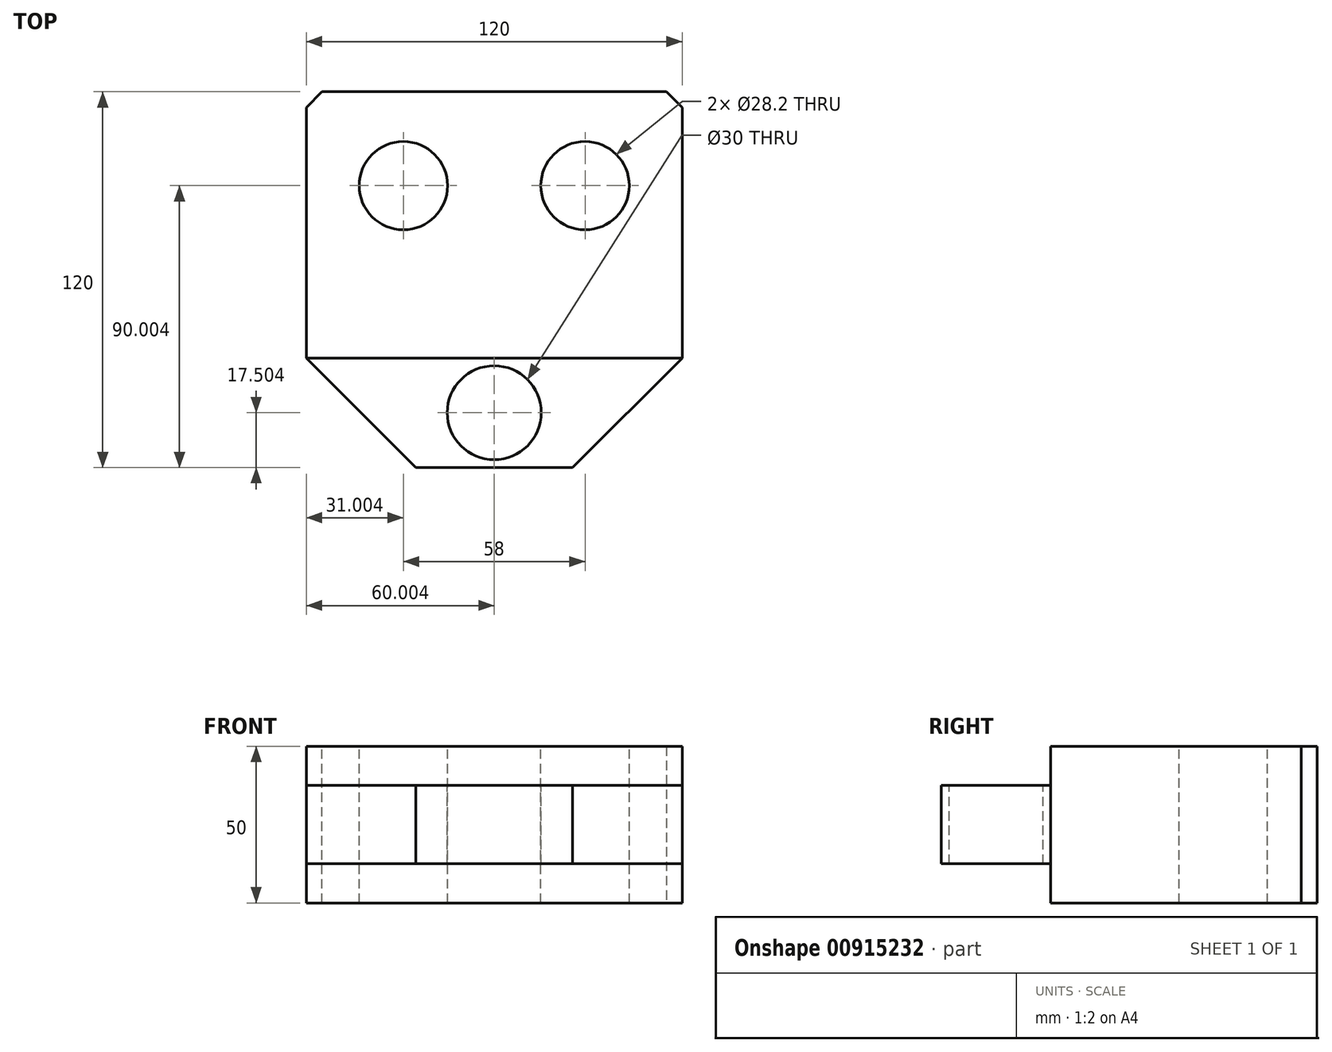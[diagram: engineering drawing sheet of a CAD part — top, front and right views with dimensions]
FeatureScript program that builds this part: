
annotation { "Feature Type Name" : "Feature", "Feature Type Description" : "" }
export const myFeature = defineFeature(function(context is Context, id is Id, definition is map)
    precondition{}
    {
        {
            var Q0;
            Q0=qCreatedBy(makeId("Top.planeOp"),FACE);
            var sketch = newSketch(context, id + "F0", { "sketchPlane" : qUnion([Q0])});
            skLineSegment(sketch, "E0.bottom", {"start": v(-56.18, 53.34) * mm, "end": v(63.82, 53.34) * mm});
            skLineSegment(sketch, "E0.top", {"start": v(-56.18, -66.66) * mm, "end": v(63.82, -66.66) * mm});
            skLineSegment(sketch, "E0.left", {"start": v(-56.18, 53.34) * mm, "end": v(-56.18, -66.66) * mm});
            skLineSegment(sketch, "E0.right", {"start": v(63.82, 53.34) * mm, "end": v(63.82, -66.66) * mm});
            skSolve(sketch);
        }
        {
            var Q0;
            Q0=makeQuery(id+"F0.imprint","IMPRINT",FACE,{"disambiguationData":[TD([[makeQuery(id+"F0.imprint","IMPRINT",EDGE,{"derivedFrom":sQuery(id+"F0.wireOp",EDGE,"E0.bottom")}),-1.0]])]});
            extrude(context, id + "F1", {"entities" : qUnion([Q0]), "depth" : 50 * mm, "offsetDistance" : 25 * mm});
        }
        {
            var Q0;
            Q0=makeQuery(id+"F1.opExtrude","SWEPT_EDGE",EDGE,{"disambiguationData":[OSD([sQuery(id+"F0.wireOp",EDGE,"E0.top"),sQuery(id+"F0.wireOp",EDGE,"E0.left")])]});
            var Q1;
            Q1=makeQuery(id+"F1.opExtrude","SWEPT_EDGE",EDGE,{"disambiguationData":[OSD([sQuery(id+"F0.wireOp",EDGE,"E0.top"),sQuery(id+"F0.wireOp",EDGE,"E0.right")])]});
            chamfer(context, id + "F2", {"entities" : qUnion([Q0, Q1]), "width" : 35 * mm, "tangentPropagation" : true});
        }
        {
            var Q0;
            Q0=makeQuery(id+"F1.opExtrude","CAP_FACE",FACE,{"disambiguationData":[OSD([sQuery(id+"F0.wireOp",EDGE,"E0.bottom"),sQuery(id+"F0.wireOp",EDGE,"E0.top"),sQuery(id+"F0.wireOp",EDGE,"E0.left"),sQuery(id+"F0.wireOp",EDGE,"E0.right")])],"isStart":false});
            var sketch = newSketch(context, id + "F3", { "sketchPlane" : qUnion([Q0])});
            skLineSegment(sketch, "E1", {"start": v(-56.18, -31.66) * mm, "end": v(63.82, -31.66) * mm});
            skLineSegment(sketch, "E2", {"start": v(63.82, -31.66) * mm, "end": v(28.82, -66.66) * mm});
            skLineSegment(sketch, "E3", {"start": v(28.82, -66.66) * mm, "end": v(-21.18, -66.66) * mm});
            skLineSegment(sketch, "E4", {"start": v(-21.18, -66.66) * mm, "end": v(-56.18, -31.66) * mm});
            skSolve(sketch);
        }
        {
            var Q0;
            Q0=makeQuery(id+"F3.imprint","IMPRINT",FACE,{"disambiguationData":[TD([[makeQuery(id+"F3.imprint","IMPRINT",EDGE,{"derivedFrom":sQuery(id+"F3.wireOp",EDGE,"E1")}),-1.0]])]});
            extrude(context, id + "F4", {"entities" : qUnion([Q0]), "operationType" : NewBodyOperationType.REMOVE, "oppositeDirection" : true, "depth" : 12.5 * mm, "offsetDistance" : 25 * mm});
        }
        {
            var Q0;
            Q0=makeQuery(id+"F1.opExtrude","CAP_FACE",FACE,{"disambiguationData":[OSD([sQuery(id+"F0.wireOp",EDGE,"E0.bottom"),sQuery(id+"F0.wireOp",EDGE,"E0.top"),sQuery(id+"F0.wireOp",EDGE,"E0.left"),sQuery(id+"F0.wireOp",EDGE,"E0.right")])],"isStart":true});
            var sketch = newSketch(context, id + "F5", { "sketchPlane" : qUnion([Q0])});
            skLineSegment(sketch, "E5", {"start": v(63.82, 31.66) * mm, "end": v(-56.18, 31.66) * mm});
            skLineSegment(sketch, "E6", {"start": v(-56.18, 31.66) * mm, "end": v(-21.18, 66.66) * mm});
            skLineSegment(sketch, "E7", {"start": v(-21.18, 66.66) * mm, "end": v(28.82, 66.66) * mm});
            skLineSegment(sketch, "E8", {"start": v(28.82, 66.66) * mm, "end": v(63.82, 31.66) * mm});
            skSolve(sketch);
        }
        {
            var Q0;
            Q0=makeQuery(id+"F5.imprint","IMPRINT",FACE,{"disambiguationData":[TD([[makeQuery(id+"F5.imprint","IMPRINT",EDGE,{"derivedFrom":sQuery(id+"F5.wireOp",EDGE,"E5")}),-1.0]])]});
            extrude(context, id + "F6", {"entities" : qUnion([Q0]), "operationType" : NewBodyOperationType.REMOVE, "oppositeDirection" : true, "depth" : 12.5 * mm, "offsetDistance" : 25 * mm});
        }
        {
            var Q0;
            Q0=makeQuery(id+"F4.boolean.opBoolean","COPY",FACE,{"derivedFrom":makeQuery(id+"F4.opExtrude","CAP_FACE",FACE,{"disambiguationData":[OSD([sQuery(id+"F3.wireOp",EDGE,"E1"),sQuery(id+"F3.wireOp",EDGE,"E2"),sQuery(id+"F3.wireOp",EDGE,"E3"),sQuery(id+"F3.wireOp",EDGE,"E4")])],"isStart":false})});
            var sketch = newSketch(context, id + "F7", { "sketchPlane" : qUnion([Q0])});
            skLineSegment(sketch, "E9", {"start": v(3.82, -66.66) * mm, "end": v(3.82, -31.66) * mm, "construction": true});
            skLineSegment(sketch, "E10", {"start": v(-38.68, -49.16) * mm, "end": v(46.32, -49.16) * mm, "construction": true});
            skCircle(sketch, "E11", {"center": v(3.82, -49.16) * mm, "radius": 15 * mm});
            skSolve(sketch);
        }
        {
            var Q0;
            Q0=makeQuery(id+"F7.imprint","IMPRINT",FACE,{"disambiguationData":[TD([[makeQuery(id+"F7.imprint","IMPRINT",EDGE,{"derivedFrom":sQuery(id+"F7.wireOp",EDGE,"E11")}),1.0]])]});
            extrude(context, id + "F8", {"entities" : qUnion([Q0]), "operationType" : NewBodyOperationType.REMOVE, "endBound" : BoundingType.THROUGH_ALL, "oppositeDirection" : true, "depth" : 25 * mm, "offsetDistance" : 25 * mm});
        }
        {
            var Q0;
            Q0=makeQuery(id+"F1.opExtrude","CAP_FACE",FACE,{"disambiguationData":[OSD([sQuery(id+"F0.wireOp",EDGE,"E0.bottom"),sQuery(id+"F0.wireOp",EDGE,"E0.top"),sQuery(id+"F0.wireOp",EDGE,"E0.left"),sQuery(id+"F0.wireOp",EDGE,"E0.right")])],"isStart":false});
            var sketch = newSketch(context, id + "F9", { "sketchPlane" : qUnion([Q0])});
            skCircle(sketch, "E12", {"center": v(-25.18, 23.34) * mm, "radius": 14.1 * mm});
            skCircle(sketch, "E13", {"center": v(32.82, 23.34) * mm, "radius": 14.1 * mm});
            skLineSegment(sketch, "E14", {"start": v(3.82, 53.34) * mm, "end": v(3.82, -31.66) * mm, "construction": true});
            skSolve(sketch);
        }
        {
            var Q0;
            Q0=makeQuery(id+"F9.imprint","IMPRINT",FACE,{"disambiguationData":[TD([[makeQuery(id+"F9.imprint","IMPRINT",EDGE,{"derivedFrom":sQuery(id+"F9.wireOp",EDGE,"E12")}),1.0]])]});
            var Q1;
            Q1=makeQuery(id+"F9.imprint","IMPRINT",FACE,{"disambiguationData":[TD([[makeQuery(id+"F9.imprint","IMPRINT",EDGE,{"derivedFrom":sQuery(id+"F9.wireOp",EDGE,"E13")}),1.0]])]});
            extrude(context, id + "F10", {"entities" : qUnion([Q0, Q1]), "operationType" : NewBodyOperationType.REMOVE, "endBound" : BoundingType.THROUGH_ALL, "oppositeDirection" : true, "depth" : 25 * mm, "offsetDistance" : 25 * mm});
        }
        {
            var Q0;
            Q0=makeQuery(id+"F1.opExtrude","SWEPT_EDGE",EDGE,{"disambiguationData":[OSD([sQuery(id+"F0.wireOp",EDGE,"E0.bottom"),sQuery(id+"F0.wireOp",EDGE,"E0.right")])]});
            var Q1;
            Q1=makeQuery(id+"F1.opExtrude","SWEPT_EDGE",EDGE,{"disambiguationData":[OSD([sQuery(id+"F0.wireOp",EDGE,"E0.bottom"),sQuery(id+"F0.wireOp",EDGE,"E0.left")])]});
            chamfer(context, id + "F11", {"entities" : qUnion([Q0, Q1]), "width" : 5 * mm, "tangentPropagation" : true});
        }
    });
